# Revit family: CITY
name_source: partatom
category: Lighting Fixtures
units: mm (PartAtom-declared; Revit-internal decimal feet)

## family parameters
Cut with Voids When Loaded = No
Host = Face
Light Source = Yes
Maintain Annotation Orientation = Yes
Part Type = Normal
Room Calculation Point = No
Round Connector Dimension = Use Diameter
Shared = No

## types (10) — shared parameters
Color Filter = 16777215
Default Elevation = 1219 mm
Dimming Lamp Color Temperature Shift = <None>
Emit from Line Length = 610 mm
Tilt Angle = -90.00°
zero-valued in all types: LuxLight_Alto, LuxLight_AltoAreaLuminosa, LuxLight_Amperios, LuxLight_Ancho, LuxLight_AnchoAreaLuminosa, LuxLight_Diametro, LuxLight_DiametroAreaLuminosa, LuxLight_Largo, LuxLight_LargoAreaLuminosa, LuxLight_ProtuberanciaTecho

## per-type parameters (varying)
| type | LuxLight_Lumenes | LuxLight_Temperatura | LuxLight_Watios | Manufacturer | Photometric Web File | Radio |
| LISUP0584 | 370 lm | 4000 K | 5 W |  | LISUP058401 .ies | 297 mm |
| LISUP0583 | 360 lm | 3000 K | 5 W |  | LISUP058301 .ies | 292 mm |
| LISUP1083 | 750 lm | 3000 K | 10 W |  | LISUP108301 .ies | 542 mm |
| LISUP1084 | 760 lm | 4000 K | 10 W |  | LISUP108401 .ies | 542 mm |
| LISUP2083 | 1550 lm | 3000 K | 20 W |  | LISUP208301 .ies | 1042 mm |
| LISUP2084 | 1600 lm | 4000 K | 20 W |  | LISUP208401 .ies | 1042 mm |
| LISUP3083 | 2280 lm | 3000 K | 30 W |  | LISUP308301 .ies | 1542 mm |
| LISUP3084 | 2340 lm | 4000 K | 30 W |  | LISUP308401 .ies | 1542 mm |
| LISUP80 | 5000 lm | 0 K | 50 W | LUXLIGHT | LISUP80X 50W 4000K .ies | 40 mm  [stored 0.131234 ft] |
| LISUP120 | 10000 lm | 0 K | 80 W |  | LISUP120X 80W 4000K .ies | 60 mm  [stored 0.19685 ft] |

note: [stored X ft] marks values corroborated as IEEE doubles in the binary element streams (Revit-internal decimal feet)

## geometry (parser evidence)
native form markers: Sweep x6
no freeform markers — native parametric forms only
